# Revit family: KYRA 010-SBC-010B
name_source: partatom
category: Plumbing Fixtures
revit_build: Autodesk Revit 2017 (Build: 20171027_0315(x64)
units: mm (PartAtom-declared; Revit-internal decimal feet)

## family parameters
Always vertical = Yes
Cut with Voids When Loaded = No
OmniClass Number = 23.45.00.00
OmniClass Title = Sanitary, Laundry, and Cleaning Equipment
Part Type = Normal
Room Calculation Point = No
Round Connector Dimension = Use Diameter
Shared = No
Work Plane-Based = No

## types (4) — shared parameters
Manufacturer = SEIMA
URL = www.seima.com.au
Waste Connection = Yes
Waste Size = 32 mm

## per-type parameters (varying)
| type | Basin Material | Chrome | Model |
| 191001 | Porcelin | CHROME | KYRA SBC-010B |
| 191002 | Vitreous china_Soft grey | Porcelin | TYRIA |
| 191003 | Vitreous china_Sand colour | Porcelin | TYRIA |
| 191004 | Vitreous china_Black stone | Porcelin | TYRIA |

## geometry (parser evidence)
native form markers: Sweep x2
no freeform markers — native parametric forms only
